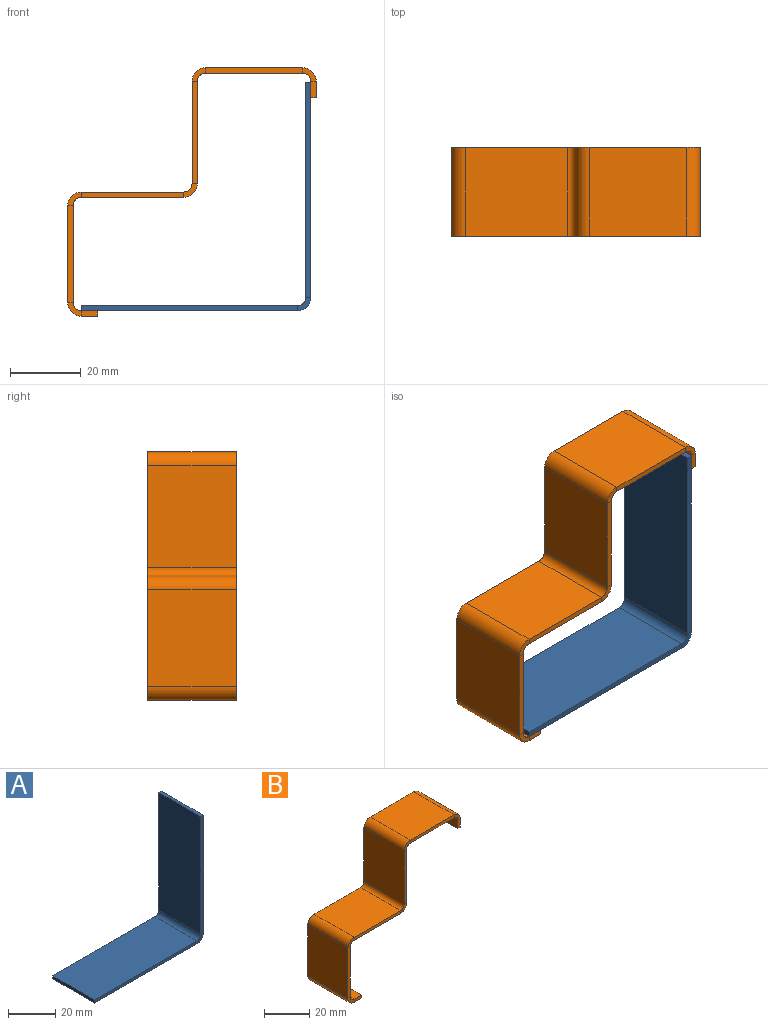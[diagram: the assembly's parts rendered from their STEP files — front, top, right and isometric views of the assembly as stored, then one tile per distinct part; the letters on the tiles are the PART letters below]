
ASSEMBLY  parts=2 mates=1
PART A: 14 faces, bbox 64.7x25x64.5 mm
  f0: plane 60.9x1.5mm, normal (0,1,0), area 91.4mm2, adj f2,f3,f4,f11
  f1: plane 60.9x1.5mm, normal (0,-1,0), area 91.4mm2, adj f2,f3,f4,f10
  f2: plane 25x1.5mm, normal (-1,0,0), area 37.5mm2, adj f0,f1,f3,f4
  f3: plane 60.9x25mm, normal (0,0,-1), area 1522.5mm2, adj f0,f1,f2,f12
  f4: plane 60.9x25mm, normal (0,0,1), area 1522.5mm2, adj f0,f1,f2,f13
  f5: plane 60.7x1.5mm, normal (0,1,0), area 91mm2, adj f6,f8,f9,f11
  f6: plane 25x1.5mm, normal (0,0,1), area 37.5mm2, adj f5,f7,f8,f9
  f7: plane 60.7x1.5mm, normal (0,-1,0), area 91mm2, adj f6,f8,f9,f10
  f8: plane 60.7x25mm, normal (1,0,0), area 1517.5mm2, adj f5,f6,f7,f12
  f9: plane 60.7x25mm, normal (-1,0,0), area 1517.5mm2, adj f5,f6,f7,f13
  f10: plane 3.8x3.8mm, normal (0,-1,0), area 7.2mm2, adj f1,f7,f12,f13
  f11: plane 3.8x3.8mm, normal (0,1,0), area 7.2mm2, adj f0,f5,f12,f13
  f12: cylinder r=3.8mm len=25mm, axis (0,-1,0), area 149.2mm2, adj f3,f8,f10,f11
  f13: cylinder r=2.3mm len=25mm, axis (0,-1,0), area 90.3mm2, adj f4,f9,f10,f11
PART B: 46 faces, bbox 70x25x70 mm
  f0: plane 4.7x1.5mm, normal (0,1,0), area 7.1mm2, adj f2,f3,f4,f43
  f1: plane 4.7x1.5mm, normal (0,-1,0), area 7.1mm2, adj f2,f3,f4,f42
  f2: plane 25x1.5mm, normal (0,0,-1), area 37.5mm2, adj f0,f1,f3,f4
  f3: plane 25x4.7mm, normal (1,0,0), area 117.5mm2, adj f0,f1,f2,f44
  f4: plane 25x4.7mm, normal (-1,0,0), area 117.5mm2, adj f0,f1,f2,f45
  f5: plane 27.4x1.5mm, normal (0,1,0), area 41.1mm2, adj f7,f8,f39,f43
  f6: plane 27.4x1.5mm, normal (0,-1,0), area 41.1mm2, adj f7,f8,f38,f42
  f7: plane 27.4x25mm, normal (0,0,1), area 685mm2, adj f5,f6,f40,f44
  f8: plane 27.4x25mm, normal (0,0,-1), area 685mm2, adj f5,f6,f41,f45
  f9: plane 28.9x1.5mm, normal (0,1,0), area 43.4mm2, adj f11,f12,f35,f39
  f10: plane 28.9x1.5mm, normal (0,-1,0), area 43.4mm2, adj f11,f12,f34,f38
  f11: plane 28.9x25mm, normal (-1,0,0), area 722.5mm2, adj f9,f10,f37,f40
  f12: plane 28.9x25mm, normal (1,0,0), area 722.5mm2, adj f9,f10,f36,f41
  f13: plane 28.9x1.5mm, normal (0,1,0), area 43.3mm2, adj f15,f16,f31,f35
  f14: plane 28.9x1.5mm, normal (0,-1,0), area 43.3mm2, adj f15,f16,f30,f34
  f15: plane 28.9x25mm, normal (0,0,1), area 722.5mm2, adj f13,f14,f32,f37
  f16: plane 28.9x25mm, normal (0,0,-1), area 722.5mm2, adj f13,f14,f33,f36
  f17: plane 27.4x1.5mm, normal (0,1,0), area 41.1mm2, adj f19,f20,f27,f31
  f18: plane 27.4x1.5mm, normal (0,-1,0), area 41.1mm2, adj f19,f20,f26,f30
  f19: plane 27.4x25mm, normal (-1,0,0), area 685mm2, adj f17,f18,f28,f32
  f20: plane 27.4x25mm, normal (1,0,0), area 685mm2, adj f17,f18,f29,f33
  f21: plane 4.7x1.5mm, normal (0,1,0), area 7.1mm2, adj f22,f24,f25,f27
  f22: plane 25x1.5mm, normal (1,0,0), area 37.5mm2, adj f21,f23,f24,f25
  f23: plane 4.7x1.5mm, normal (0,-1,0), area 7.1mm2, adj f22,f24,f25,f26
  f24: plane 25x4.7mm, normal (0,0,-1), area 117.5mm2, adj f21,f22,f23,f28
  f25: plane 25x4.7mm, normal (0,0,1), area 117.5mm2, adj f21,f22,f23,f29
  f26: plane 3.8x3.8mm, normal (0,-1,0), area 7.2mm2, adj f18,f23,f28,f29
  f27: plane 3.8x3.8mm, normal (0,1,0), area 7.2mm2, adj f17,f21,f28,f29
  f28: cylinder r=3.8mm len=25mm, axis (0,-1,0), area 149.2mm2, adj f19,f24,f26,f27
  f29: cylinder r=2.3mm len=25mm, axis (0,-1,0), area 90.3mm2, adj f20,f25,f26,f27
  f30: plane 3.8x3.8mm, normal (0,-1,0), area 7.2mm2, adj f14,f18,f32,f33
  f31: plane 3.8x3.8mm, normal (0,1,0), area 7.2mm2, adj f13,f17,f32,f33
  f32: cylinder r=3.8mm len=25mm, axis (0,-1,0), area 149.2mm2, adj f15,f19,f30,f31
  f33: cylinder r=2.3mm len=25mm, axis (0,-1,0), area 90.3mm2, adj f16,f20,f30,f31
  f34: plane 3.8x3.8mm, normal (0,-1,0), area 7.2mm2, adj f10,f14,f36,f37
  f35: plane 3.8x3.8mm, normal (0,1,0), area 7.2mm2, adj f9,f13,f36,f37
  f36: cylinder r=3.8mm len=25mm, axis (0,-1,0), area 149.2mm2, adj f12,f16,f34,f35
  f37: cylinder r=2.3mm len=25mm, axis (0,-1,0), area 90.3mm2, adj f11,f15,f34,f35
  f38: plane 3.8x3.8mm, normal (0,-1,0), area 7.2mm2, adj f6,f10,f40,f41
  f39: plane 3.8x3.8mm, normal (0,1,0), area 7.2mm2, adj f5,f9,f40,f41
  f40: cylinder r=3.8mm len=25mm, axis (0,-1,0), area 149.2mm2, adj f7,f11,f38,f39
  f41: cylinder r=2.3mm len=25mm, axis (0,-1,0), area 90.3mm2, adj f8,f12,f38,f39
  f42: plane 3.8x3.8mm, normal (0,-1,0), area 7.2mm2, adj f1,f6,f44,f45
  f43: plane 3.8x3.8mm, normal (0,1,0), area 7.2mm2, adj f0,f5,f44,f45
  f44: cylinder r=3.8mm len=25mm, axis (0,-1,0), area 149.2mm2, adj f3,f7,f42,f43
  f45: cylinder r=2.3mm len=25mm, axis (0,-1,0), area 90.3mm2, adj f4,f8,f42,f43
PLACE A t=(-41.36,-22.02,-19.05)mm
PLACE B t=(-19.03,-22.02,8.64)mm
MATE fastened A.f3 <-> B.f25  axis (0,0,-1) through (-76.76,-47.02,-45.83)mm
